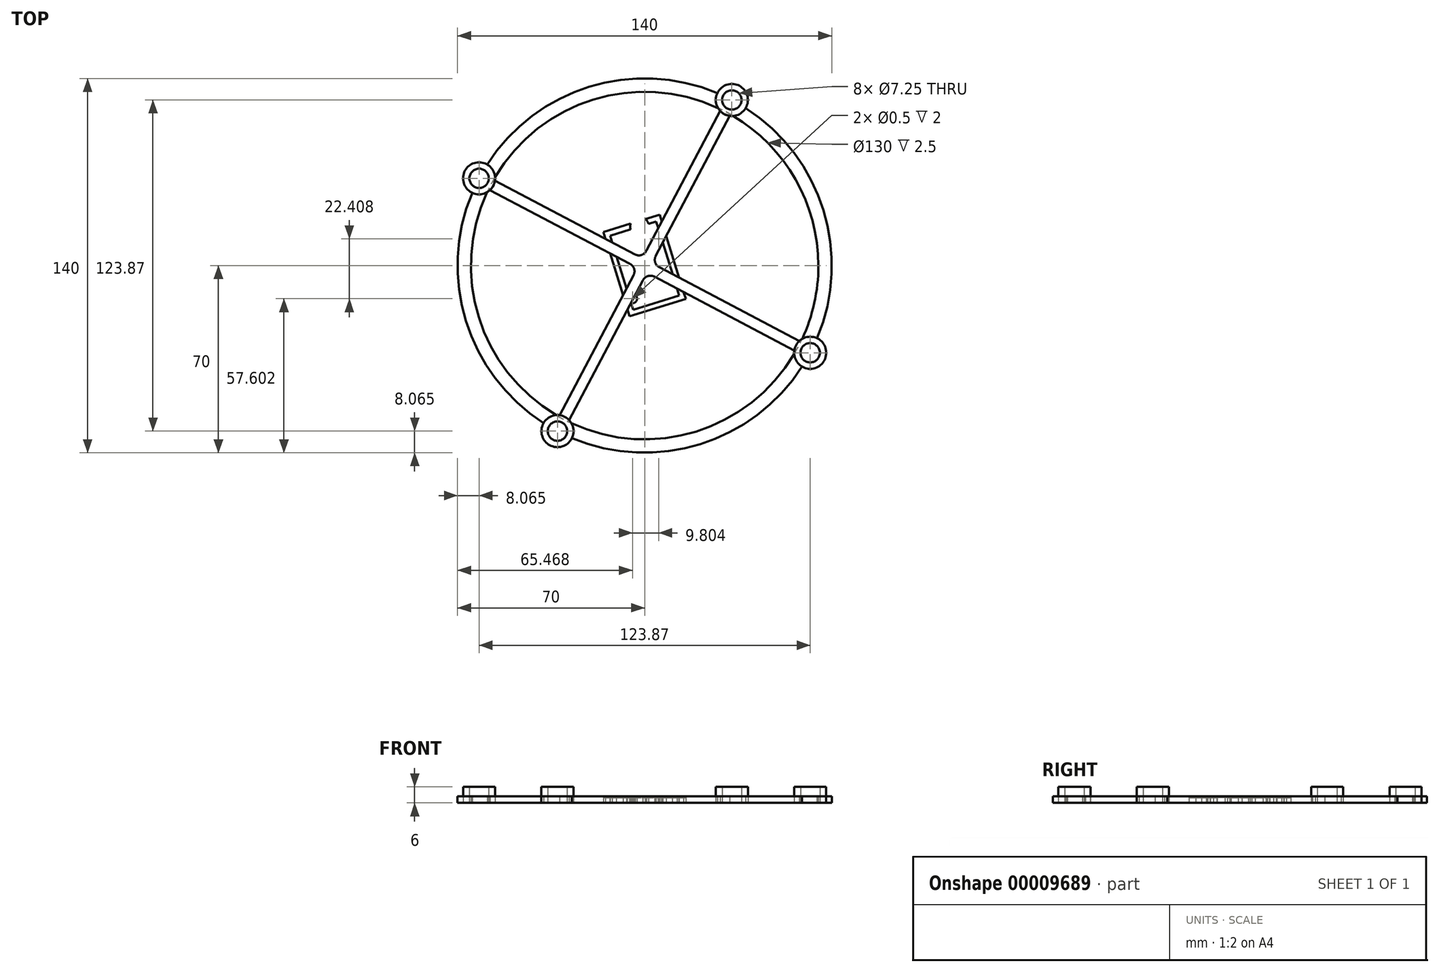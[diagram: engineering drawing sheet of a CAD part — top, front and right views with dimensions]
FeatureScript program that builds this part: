
annotation { "Feature Type Name" : "Feature", "Feature Type Description" : "" }
export const myFeature = defineFeature(function(context is Context, id is Id, definition is map)
    precondition{}
    {
        {
            var Q0;
            Q0=qCreatedBy(makeId("Top.planeOp"),FACE);
            var sketch = newSketch(context, id + "F0", { "sketchPlane" : qUnion([Q0])});
            skCircle(sketch, "E0", {"center": v(-61.93, 32.62) * mm, "radius": 3.62 * mm});
            skCircle(sketch, "E1", {"center": v(-61.93, 32.62) * mm, "radius": 6 * mm});
            skCircle(sketch, "E2", {"center": v(0, 0) * mm, "radius": 70 * mm});
            skCircle(sketch, "E3", {"center": v(0, 0) * mm, "radius": 65 * mm});
            skCircle(sketch, "E4.1.0", {"center": v(-32.62, -61.93) * mm, "radius": 3.62 * mm});
            skCircle(sketch, "E4.1.1", {"center": v(-32.62, -61.93) * mm, "radius": 6 * mm});
            skCircle(sketch, "E4.2.0", {"center": v(61.93, -32.62) * mm, "radius": 3.62 * mm});
            skCircle(sketch, "E4.2.1", {"center": v(61.93, -32.62) * mm, "radius": 6 * mm});
            skCircle(sketch, "E4.3.0", {"center": v(32.62, 61.93) * mm, "radius": 3.62 * mm});
            skCircle(sketch, "E4.3.1", {"center": v(32.62, 61.93) * mm, "radius": 6 * mm});
            skLineSegment(sketch, "E5", {"start": v(32.62, 61.93) * mm, "end": v(-32.62, -61.93) * mm});
            skLineSegment(sketch, "E6", {"start": v(-56.55, 32.05) * mm, "end": v(-3.59, 4.15) * mm});
            skArc(sketch, "E7", {"start": v(-3.59, 4.15) * mm, "mid": v(-1.1, 3.97) * mm, "end": v(0.72, 5.66) * mm});
            skLineSegment(sketch, "E8", {"start": v(0.72, 5.66) * mm, "end": v(28.5, 58.42) * mm});
            skLineSegment(sketch, "E9", {"start": v(61.93, -32.62) * mm, "end": v(-61.93, 32.62) * mm});
            skLineSegment(sketch, "E10.1.0", {"start": v(-5.66, 0.72) * mm, "end": v(-58.42, 28.5) * mm});
            skArc(sketch, "E10.1.1", {"start": v(-4.15, -3.59) * mm, "mid": v(-3.97, -1.1) * mm, "end": v(-5.66, 0.72) * mm});
            skLineSegment(sketch, "E10.1.2", {"start": v(-32.05, -56.55) * mm, "end": v(-4.15, -3.59) * mm});
            skLineSegment(sketch, "E10.2.0", {"start": v(-0.72, -5.66) * mm, "end": v(-28.5, -58.42) * mm});
            skArc(sketch, "E10.2.1", {"start": v(3.59, -4.15) * mm, "mid": v(1.1, -3.97) * mm, "end": v(-0.72, -5.66) * mm});
            skLineSegment(sketch, "E10.2.2", {"start": v(56.55, -32.05) * mm, "end": v(3.59, -4.15) * mm});
            skLineSegment(sketch, "E10.3.0", {"start": v(5.66, -0.72) * mm, "end": v(58.42, -28.5) * mm});
            skArc(sketch, "E10.3.1", {"start": v(4.15, 3.59) * mm, "mid": v(3.97, 1.1) * mm, "end": v(5.66, -0.72) * mm});
            skLineSegment(sketch, "E10.3.2", {"start": v(32.05, 56.55) * mm, "end": v(4.15, 3.59) * mm});
            skSolve(sketch);
        }
        {
            var Q0;
            {var subQ0=sQuery(id+"F0.wireOp",EDGE,"E2");var subQ1=sQuery(id+"F0.wireOp",EDGE,"E0");var subQ2=makeQuery(id+"F0.imprint","INTERSECT",VERTEX,{"disambiguationData":[OD(0.0)],"derivedFrom":[subQ1,subQ0]});Q0=makeQuery(id+"F0.imprint","IMPRINT",FACE,{"disambiguationData":[TD([[makeQuery(id+"F0.imprint","IMPRINT",EDGE,{"disambiguationData":[TD([[subQ2,1.0]])],"derivedFrom":subQ1}),-1.0]])]});}
            var Q1;
            {var subQ3=sQuery(id+"F0.wireOp",EDGE,"E0");var subQ8=sQuery(id+"F0.wireOp",EDGE,"E2");var subQ9=makeQuery(id+"F0.imprint","INTERSECT",VERTEX,{"disambiguationData":[OD(0.0)],"derivedFrom":[subQ3,subQ8]});Q1=makeQuery(id+"F0.imprint","IMPRINT",FACE,{"disambiguationData":[TD([[makeQuery(id+"F0.imprint","IMPRINT",EDGE,{"disambiguationData":[TD([[subQ9,-1.0]])],"derivedFrom":subQ3}),-1.0]])]});}
            var Q2;
            {var subQ3=sQuery(id+"F0.wireOp",EDGE,"E0");var subQ8=sQuery(id+"F0.wireOp",EDGE,"E2");var subQ9=makeQuery(id+"F0.imprint","INTERSECT",VERTEX,{"disambiguationData":[OD(1.0)],"derivedFrom":[subQ3,subQ8]});Q2=makeQuery(id+"F0.imprint","IMPRINT",FACE,{"disambiguationData":[TD([[makeQuery(id+"F0.imprint","IMPRINT",EDGE,{"disambiguationData":[TD([[subQ9,1.0]])],"derivedFrom":subQ3}),-1.0]])]});}
            var Q3;
            {var subQ0=sQuery(id+"F0.wireOp",EDGE,"E9");var subQ3=sQuery(id+"F0.wireOp",EDGE,"E1");var subQ4=makeQuery(id+"F0.imprint","INTERSECT",VERTEX,{"derivedFrom":[subQ3,subQ0]});Q3=makeQuery(id+"F0.imprint","IMPRINT",FACE,{"disambiguationData":[TD([[makeQuery(id+"F0.imprint","IMPRINT",EDGE,{"disambiguationData":[TD([[subQ4,-1.0]])],"derivedFrom":subQ3}),1.0]])]});}
            var Q4;
            {var subQ0=sQuery(id+"F0.wireOp",EDGE,"E10.1.0");var subQ1=sQuery(id+"F0.wireOp",EDGE,"E1");var subQ2=makeQuery(id+"F0.imprint","INTERSECT",VERTEX,{"derivedFrom":[subQ1,subQ0]});Q4=makeQuery(id+"F0.imprint","IMPRINT",FACE,{"disambiguationData":[TD([[makeQuery(id+"F0.imprint","IMPRINT",EDGE,{"disambiguationData":[TD([[subQ2,-1.0]])],"derivedFrom":subQ1}),1.0]])]});}
            var Q5;
            {var subQ1=sQuery(id+"F0.wireOp",EDGE,"E1");var subQ3=sQuery(id+"F0.wireOp",EDGE,"E3");var subQ5=makeQuery(id+"F0.imprint","INTERSECT",VERTEX,{"disambiguationData":[OD(0.0)],"derivedFrom":[subQ1,subQ3]});Q5=makeQuery(id+"F0.imprint","IMPRINT",FACE,{"disambiguationData":[TD([[makeQuery(id+"F0.imprint","IMPRINT",EDGE,{"disambiguationData":[TD([[subQ5,1.0]])],"derivedFrom":subQ1}),1.0]])]});}
            var Q6;
            {var subQ1=sQuery(id+"F0.wireOp",EDGE,"E1");var subQ3=sQuery(id+"F0.wireOp",EDGE,"E3");var subQ5=makeQuery(id+"F0.imprint","INTERSECT",VERTEX,{"disambiguationData":[OD(1.0)],"derivedFrom":[subQ1,subQ3]});Q6=makeQuery(id+"F0.imprint","IMPRINT",FACE,{"disambiguationData":[TD([[makeQuery(id+"F0.imprint","IMPRINT",EDGE,{"disambiguationData":[TD([[subQ5,-1.0]])],"derivedFrom":subQ1}),1.0]])]});}
            var Q7;
            {var subQ0=sQuery(id+"F0.wireOp",EDGE,"E4.3.1");var subQ1=sQuery(id+"F0.wireOp",EDGE,"E2");var subQ3=makeQuery(id+"F0.imprint","INTERSECT",VERTEX,{"disambiguationData":[OD(0.0)],"derivedFrom":[subQ1,subQ0]});Q7=makeQuery(id+"F0.imprint","IMPRINT",FACE,{"disambiguationData":[TD([[makeQuery(id+"F0.imprint","IMPRINT",EDGE,{"disambiguationData":[TD([[subQ3,-1.0]])],"derivedFrom":subQ1}),-1.0]])]});}
            var Q8;
            {var subQ5=sQuery(id+"F0.wireOp",EDGE,"E4.3.1");var subQ7=sQuery(id+"F0.wireOp",EDGE,"E2");var subQ8=makeQuery(id+"F0.imprint","INTERSECT",VERTEX,{"disambiguationData":[OD(0.0)],"derivedFrom":[subQ7,subQ5]});Q8=makeQuery(id+"F0.imprint","IMPRINT",FACE,{"disambiguationData":[TD([[makeQuery(id+"F0.imprint","IMPRINT",EDGE,{"disambiguationData":[TD([[subQ8,-1.0]])],"derivedFrom":subQ7}),1.0]])]});}
            var Q9;
            {var subQ0=sQuery(id+"F0.wireOp",EDGE,"E10.3.2");var subQ3=sQuery(id+"F0.wireOp",EDGE,"E3");var subQ4=makeQuery(id+"F0.imprint","INTERSECT",VERTEX,{"derivedFrom":[subQ3,subQ0]});Q9=makeQuery(id+"F0.imprint","IMPRINT",FACE,{"disambiguationData":[TD([[makeQuery(id+"F0.imprint","IMPRINT",EDGE,{"disambiguationData":[TD([[subQ4,-1.0]])],"derivedFrom":subQ3}),1.0]])]});}
            var Q10;
            {var subQ5=sQuery(id+"F0.wireOp",EDGE,"E4.3.1");var subQ7=sQuery(id+"F0.wireOp",EDGE,"E2");var subQ8=makeQuery(id+"F0.imprint","INTERSECT",VERTEX,{"disambiguationData":[OD(1.0)],"derivedFrom":[subQ7,subQ5]});Q10=makeQuery(id+"F0.imprint","IMPRINT",FACE,{"disambiguationData":[TD([[makeQuery(id+"F0.imprint","IMPRINT",EDGE,{"disambiguationData":[TD([[subQ8,1.0]])],"derivedFrom":subQ7}),1.0]])]});}
            var Q11;
            {var subQ0=sQuery(id+"F0.wireOp",EDGE,"E10.3.2");var subQ3=sQuery(id+"F0.wireOp",EDGE,"E3");var subQ4=makeQuery(id+"F0.imprint","INTERSECT",VERTEX,{"derivedFrom":[subQ3,subQ0]});Q11=makeQuery(id+"F0.imprint","IMPRINT",FACE,{"disambiguationData":[TD([[makeQuery(id+"F0.imprint","IMPRINT",EDGE,{"disambiguationData":[TD([[subQ4,1.0]])],"derivedFrom":subQ3}),1.0]])]});}
            var Q12;
            {var subQ0=sQuery(id+"F0.wireOp",EDGE,"E8");var subQ3=sQuery(id+"F0.wireOp",EDGE,"E3");var subQ4=makeQuery(id+"F0.imprint","INTERSECT",VERTEX,{"derivedFrom":[subQ3,subQ0]});Q12=makeQuery(id+"F0.imprint","IMPRINT",FACE,{"disambiguationData":[TD([[makeQuery(id+"F0.imprint","IMPRINT",EDGE,{"disambiguationData":[TD([[subQ4,1.0]])],"derivedFrom":subQ3}),1.0]])]});}
            var Q13;
            {var subQ0=sQuery(id+"F0.wireOp",EDGE,"E8");var subQ3=sQuery(id+"F0.wireOp",EDGE,"E3");var subQ4=makeQuery(id+"F0.imprint","INTERSECT",VERTEX,{"derivedFrom":[subQ3,subQ0]});Q13=makeQuery(id+"F0.imprint","IMPRINT",FACE,{"disambiguationData":[TD([[makeQuery(id+"F0.imprint","IMPRINT",EDGE,{"disambiguationData":[TD([[subQ4,-1.0]])],"derivedFrom":subQ3}),1.0]])]});}
            var Q14;
            {var subQ0=sQuery(id+"F0.wireOp",EDGE,"E4.2.1");var subQ1=sQuery(id+"F0.wireOp",EDGE,"E2");var subQ3=makeQuery(id+"F0.imprint","INTERSECT",VERTEX,{"disambiguationData":[OD(0.0)],"derivedFrom":[subQ1,subQ0]});Q14=makeQuery(id+"F0.imprint","IMPRINT",FACE,{"disambiguationData":[TD([[makeQuery(id+"F0.imprint","IMPRINT",EDGE,{"disambiguationData":[TD([[subQ3,-1.0]])],"derivedFrom":subQ1}),-1.0]])]});}
            var Q15;
            {var subQ5=sQuery(id+"F0.wireOp",EDGE,"E2");var subQ7=sQuery(id+"F0.wireOp",EDGE,"E4.2.1");var subQ10=makeQuery(id+"F0.imprint","INTERSECT",VERTEX,{"disambiguationData":[OD(1.0)],"derivedFrom":[subQ5,subQ7]});Q15=makeQuery(id+"F0.imprint","IMPRINT",FACE,{"disambiguationData":[TD([[makeQuery(id+"F0.imprint","IMPRINT",EDGE,{"disambiguationData":[TD([[subQ10,1.0]])],"derivedFrom":subQ5}),1.0]])]});}
            var Q16;
            {var subQ0=sQuery(id+"F0.wireOp",EDGE,"E10.3.0");var subQ3=sQuery(id+"F0.wireOp",EDGE,"E3");var subQ4=makeQuery(id+"F0.imprint","INTERSECT",VERTEX,{"derivedFrom":[subQ3,subQ0]});Q16=makeQuery(id+"F0.imprint","IMPRINT",FACE,{"disambiguationData":[TD([[makeQuery(id+"F0.imprint","IMPRINT",EDGE,{"disambiguationData":[TD([[subQ4,-1.0]])],"derivedFrom":subQ3}),1.0]])]});}
            var Q17;
            {var subQ0=sQuery(id+"F0.wireOp",EDGE,"E10.3.0");var subQ3=sQuery(id+"F0.wireOp",EDGE,"E3");var subQ4=makeQuery(id+"F0.imprint","INTERSECT",VERTEX,{"derivedFrom":[subQ3,subQ0]});Q17=makeQuery(id+"F0.imprint","IMPRINT",FACE,{"disambiguationData":[TD([[makeQuery(id+"F0.imprint","IMPRINT",EDGE,{"disambiguationData":[TD([[subQ4,1.0]])],"derivedFrom":subQ3}),1.0]])]});}
            var Q18;
            {var subQ0=sQuery(id+"F0.wireOp",EDGE,"E10.2.2");var subQ3=sQuery(id+"F0.wireOp",EDGE,"E3");var subQ4=makeQuery(id+"F0.imprint","INTERSECT",VERTEX,{"derivedFrom":[subQ3,subQ0]});Q18=makeQuery(id+"F0.imprint","IMPRINT",FACE,{"disambiguationData":[TD([[makeQuery(id+"F0.imprint","IMPRINT",EDGE,{"disambiguationData":[TD([[subQ4,-1.0]])],"derivedFrom":subQ3}),1.0]])]});}
            var Q19;
            {var subQ5=sQuery(id+"F0.wireOp",EDGE,"E4.2.1");var subQ7=sQuery(id+"F0.wireOp",EDGE,"E2");var subQ8=makeQuery(id+"F0.imprint","INTERSECT",VERTEX,{"disambiguationData":[OD(0.0)],"derivedFrom":[subQ7,subQ5]});Q19=makeQuery(id+"F0.imprint","IMPRINT",FACE,{"disambiguationData":[TD([[makeQuery(id+"F0.imprint","IMPRINT",EDGE,{"disambiguationData":[TD([[subQ8,-1.0]])],"derivedFrom":subQ7}),1.0]])]});}
            var Q20;
            {var subQ0=sQuery(id+"F0.wireOp",EDGE,"E10.2.2");var subQ3=sQuery(id+"F0.wireOp",EDGE,"E3");var subQ4=makeQuery(id+"F0.imprint","INTERSECT",VERTEX,{"derivedFrom":[subQ3,subQ0]});Q20=makeQuery(id+"F0.imprint","IMPRINT",FACE,{"disambiguationData":[TD([[makeQuery(id+"F0.imprint","IMPRINT",EDGE,{"disambiguationData":[TD([[subQ4,1.0]])],"derivedFrom":subQ3}),1.0]])]});}
            var Q21;
            {var subQ5=sQuery(id+"F0.wireOp",EDGE,"E4.1.1");var subQ7=sQuery(id+"F0.wireOp",EDGE,"E2");var subQ8=makeQuery(id+"F0.imprint","INTERSECT",VERTEX,{"disambiguationData":[OD(1.0)],"derivedFrom":[subQ7,subQ5]});Q21=makeQuery(id+"F0.imprint","IMPRINT",FACE,{"disambiguationData":[TD([[makeQuery(id+"F0.imprint","IMPRINT",EDGE,{"disambiguationData":[TD([[subQ8,1.0]])],"derivedFrom":subQ7}),1.0]])]});}
            var Q22;
            {var subQ0=sQuery(id+"F0.wireOp",EDGE,"E10.2.0");var subQ3=sQuery(id+"F0.wireOp",EDGE,"E3");var subQ4=makeQuery(id+"F0.imprint","INTERSECT",VERTEX,{"derivedFrom":[subQ3,subQ0]});Q22=makeQuery(id+"F0.imprint","IMPRINT",FACE,{"disambiguationData":[TD([[makeQuery(id+"F0.imprint","IMPRINT",EDGE,{"disambiguationData":[TD([[subQ4,1.0]])],"derivedFrom":subQ3}),1.0]])]});}
            var Q23;
            {var subQ0=sQuery(id+"F0.wireOp",EDGE,"E10.2.0");var subQ3=sQuery(id+"F0.wireOp",EDGE,"E3");var subQ4=makeQuery(id+"F0.imprint","INTERSECT",VERTEX,{"derivedFrom":[subQ3,subQ0]});Q23=makeQuery(id+"F0.imprint","IMPRINT",FACE,{"disambiguationData":[TD([[makeQuery(id+"F0.imprint","IMPRINT",EDGE,{"disambiguationData":[TD([[subQ4,-1.0]])],"derivedFrom":subQ3}),1.0]])]});}
            var Q24;
            {var subQ0=sQuery(id+"F0.wireOp",EDGE,"E10.1.2");var subQ3=sQuery(id+"F0.wireOp",EDGE,"E3");var subQ4=makeQuery(id+"F0.imprint","INTERSECT",VERTEX,{"derivedFrom":[subQ3,subQ0]});Q24=makeQuery(id+"F0.imprint","IMPRINT",FACE,{"disambiguationData":[TD([[makeQuery(id+"F0.imprint","IMPRINT",EDGE,{"disambiguationData":[TD([[subQ4,-1.0]])],"derivedFrom":subQ3}),1.0]])]});}
            var Q25;
            {var subQ0=sQuery(id+"F0.wireOp",EDGE,"E10.1.2");var subQ3=sQuery(id+"F0.wireOp",EDGE,"E3");var subQ4=makeQuery(id+"F0.imprint","INTERSECT",VERTEX,{"derivedFrom":[subQ3,subQ0]});Q25=makeQuery(id+"F0.imprint","IMPRINT",FACE,{"disambiguationData":[TD([[makeQuery(id+"F0.imprint","IMPRINT",EDGE,{"disambiguationData":[TD([[subQ4,1.0]])],"derivedFrom":subQ3}),1.0]])]});}
            var Q26;
            {var subQ0=sQuery(id+"F0.wireOp",EDGE,"E4.1.1");var subQ3=sQuery(id+"F0.wireOp",EDGE,"E2");var subQ4=makeQuery(id+"F0.imprint","INTERSECT",VERTEX,{"disambiguationData":[OD(0.0)],"derivedFrom":[subQ3,subQ0]});Q26=makeQuery(id+"F0.imprint","IMPRINT",FACE,{"disambiguationData":[TD([[makeQuery(id+"F0.imprint","IMPRINT",EDGE,{"disambiguationData":[TD([[subQ4,-1.0]])],"derivedFrom":subQ3}),1.0]])]});}
            var Q27;
            {var subQ1=sQuery(id+"F0.wireOp",EDGE,"E2");var subQ4=sQuery(id+"F0.wireOp",EDGE,"E4.1.1");var subQ6=makeQuery(id+"F0.imprint","INTERSECT",VERTEX,{"disambiguationData":[OD(0.0)],"derivedFrom":[subQ1,subQ4]});Q27=makeQuery(id+"F0.imprint","IMPRINT",FACE,{"disambiguationData":[TD([[makeQuery(id+"F0.imprint","IMPRINT",EDGE,{"disambiguationData":[TD([[subQ6,-1.0]])],"derivedFrom":subQ1}),-1.0]])]});}
            extrude(context, id + "F1", {"entities" : qUnion([Q0, Q1, Q2, Q3, Q4, Q5, Q6, Q7, Q8, Q9, Q10, Q11, Q12, Q13, Q14, Q15, Q16, Q17, Q18, Q19, Q20, Q21, Q22, Q23, Q24, Q25, Q26, Q27]), "depth" : 6 * mm});
        }
        {
            var Q0;
            Q0 = qSketchRegion(id + "F0", true);
            var Q1;
            {var subQ3=sQuery(id+"F0.wireOp",EDGE,"E10.3.1");Q1=makeQuery(id+"F0.imprint","IMPRINT",FACE,{"disambiguationData":[TD([[makeQuery(id+"F0.imprint","IMPRINT",EDGE,{"derivedFrom":subQ3}),-1.0]])]});}
            var Q2;
            {var subQ3=sQuery(id+"F0.wireOp",EDGE,"E7");Q2=makeQuery(id+"F0.imprint","IMPRINT",FACE,{"disambiguationData":[TD([[makeQuery(id+"F0.imprint","IMPRINT",EDGE,{"derivedFrom":subQ3}),-1.0]])]});}
            var Q3;
            {var subQ3=sQuery(id+"F0.wireOp",EDGE,"E10.1.1");Q3=makeQuery(id+"F0.imprint","IMPRINT",FACE,{"disambiguationData":[TD([[makeQuery(id+"F0.imprint","IMPRINT",EDGE,{"derivedFrom":subQ3}),-1.0]])]});}
            var Q4;
            {var subQ3=sQuery(id+"F0.wireOp",EDGE,"E10.2.1");Q4=makeQuery(id+"F0.imprint","IMPRINT",FACE,{"disambiguationData":[TD([[makeQuery(id+"F0.imprint","IMPRINT",EDGE,{"derivedFrom":subQ3}),-1.0]])]});}
            extrude(context, id + "F2", {"entities" : qUnion([Q0, Q1, Q2, Q3, Q4]), "depth" : 2.5 * mm});
        }
        {
            var Q0;
            {var subQ3=sQuery(id+"F0.wireOp",EDGE,"E10.3.1");Q0=makeQuery(id+"F0.imprint","IMPRINT",FACE,{"disambiguationData":[TD([[makeQuery(id+"F0.imprint","IMPRINT",EDGE,{"derivedFrom":subQ3}),-1.0]])]});}
            var sketch = newSketch(context, id + "F3", { "sketchPlane" : qUnion([Q0])});
            skLineSegment(sketch, "E11", {"start": v(-32.62, -61.93) * mm, "end": v(-61.93, 32.62) * mm, "construction": true});
            skLineSegment(sketch, "E12", {"start": v(-61.93, 32.62) * mm, "end": v(32.62, 61.93) * mm, "construction": true});
            skLineSegment(sketch, "E13", {"start": v(32.62, 61.93) * mm, "end": v(61.93, -32.62) * mm, "construction": true});
            skLineSegment(sketch, "E14", {"start": v(61.93, -32.62) * mm, "end": v(-32.62, -61.93) * mm, "construction": true});
            skLineSegment(sketch, "E15", {"start": v(-4.3, -16.51) * mm, "end": v(12.9, -11.18) * mm});
            skLineSegment(sketch, "E16", {"start": v(12.9, -11.18) * mm, "end": v(4.3, 16.51) * mm});
            skLineSegment(sketch, "E17", {"start": v(4.3, 16.51) * mm, "end": v(-12.9, 11.18) * mm});
            skLineSegment(sketch, "E18", {"start": v(-12.9, 11.18) * mm, "end": v(-4.3, -16.51) * mm});
            skLineSegment(sketch, "E19.0", {"start": v(-15.4, 12.5) * mm, "end": v(-5.62, -19.02) * mm});
            skLineSegment(sketch, "E19.1", {"start": v(5.62, 19.02) * mm, "end": v(-15.4, 12.5) * mm});
            skLineSegment(sketch, "E19.2", {"start": v(15.4, -12.5) * mm, "end": v(5.62, 19.02) * mm});
            skLineSegment(sketch, "E19.3", {"start": v(-5.62, -19.02) * mm, "end": v(15.4, -12.5) * mm});
            skCircle(sketch, "E20", {"center": v(-1.9, 14.59) * mm, "radius": 3.5 * mm});
            skCircle(sketch, "E21", {"center": v(-1.9, 14.59) * mm, "radius": 5.5 * mm});
            skCircle(sketch, "E22", {"center": v(-4.53, -12.4) * mm, "radius": 1.7 * mm});
            skCircle(sketch, "E23", {"center": v(-4.53, -12.4) * mm, "radius": 0.25 * mm});
            skLineSegment(sketch, "E24", {"start": v(-4.03, -14.02) * mm, "end": v(-4.98, -14.32) * mm});
            skLineSegment(sketch, "E25", {"start": v(-5.04, -10.77) * mm, "end": v(-6, -11.07) * mm});
            skCircle(sketch, "E26", {"center": v(5.27, 10.01) * mm, "radius": 1.7 * mm});
            skCircle(sketch, "E27", {"center": v(5.27, 10.01) * mm, "radius": 0.25 * mm});
            skLineSegment(sketch, "E28", {"start": v(5.78, 8.39) * mm, "end": v(6.73, 8.68) * mm});
            skLineSegment(sketch, "E29", {"start": v(4.77, 11.63) * mm, "end": v(5.72, 11.93) * mm});
            skSolve(sketch);
        }
        {
            var Q0;
            Q0=makeQuery(id+"F3.imprint","IMPRINT",FACE,{"disambiguationData":[TD([[makeQuery(id+"F3.imprint","IMPRINT",EDGE,{"derivedFrom":sQuery(id+"F3.wireOp",EDGE,"E23")}),1.0]])]});
            var Q1;
            {var subQ0=sQuery(id+"F0.wireOp",EDGE,"E5");var subQ1=makeQuery(id+"F0.imprint","IMPRINT",EDGE,{"disambiguationData":[TD([[makeQuery(id+"F0.imprint","INTERSECT",VERTEX,{"derivedFrom":[sQuery(id+"F0.wireOp",EDGE,"E4.3.1"),subQ0]}),-1.0]])],"derivedFrom":subQ0});var subQ2=sQuery(id+"F3.wireOp",EDGE,"E27");var subQ4=makeQuery(id+"F3.imprint","INTERSECT",VERTEX,{"disambiguationData":[OD(0.0)],"derivedFrom":[subQ1,subQ2]});Q1=makeQuery(id+"F3.imprint","IMPRINT",FACE,{"disambiguationData":[TD([[makeQuery(id+"F3.imprint","IMPRINT",EDGE,{"disambiguationData":[TD([[subQ4,-1.0]])],"derivedFrom":subQ2}),1.0]])]});}
            var Q2;
            {var subQ0=sQuery(id+"F0.wireOp",EDGE,"E5");var subQ1=makeQuery(id+"F0.imprint","IMPRINT",EDGE,{"disambiguationData":[TD([[makeQuery(id+"F0.imprint","INTERSECT",VERTEX,{"derivedFrom":[sQuery(id+"F0.wireOp",EDGE,"E4.3.1"),subQ0]}),-1.0]])],"derivedFrom":subQ0});var subQ2=sQuery(id+"F3.wireOp",EDGE,"E27");var subQ4=makeQuery(id+"F3.imprint","INTERSECT",VERTEX,{"disambiguationData":[OD(0.0)],"derivedFrom":[subQ1,subQ2]});Q2=makeQuery(id+"F3.imprint","IMPRINT",FACE,{"disambiguationData":[TD([[makeQuery(id+"F3.imprint","IMPRINT",EDGE,{"disambiguationData":[TD([[subQ4,1.0]])],"derivedFrom":subQ2}),1.0]])]});}
            extrude(context, id + "F4", {"entities" : qUnion([Q0, Q1, Q2]), "operationType" : NewBodyOperationType.REMOVE, "depth" : 2 * mm});
        }
        {
            var Q0;
            {var subQ18=sQuery(id+"F3.wireOp",EDGE,"E15");Q0=makeQuery(id+"F3.imprint","IMPRINT",FACE,{"disambiguationData":[TD([[makeQuery(id+"F3.imprint","IMPRINT",EDGE,{"derivedFrom":subQ18}),-1.0]])]});}
            var Q1;
            {var subQ1=sQuery(id+"F3.wireOp",EDGE,"E17");var subQ5=sQuery(id+"F3.wireOp",EDGE,"E20");var subQ7=makeQuery(id+"F3.imprint","INTERSECT",VERTEX,{"disambiguationData":[OD(1.0)],"derivedFrom":[subQ1,subQ5]});Q1=makeQuery(id+"F3.imprint","IMPRINT",FACE,{"disambiguationData":[TD([[makeQuery(id+"F3.imprint","IMPRINT",EDGE,{"disambiguationData":[TD([[subQ7,-1.0]])],"derivedFrom":subQ1}),-1.0]])]});}
            var Q2;
            {var subQ0=sQuery(id+"F3.wireOp",EDGE,"E21");var subQ1=sQuery(id+"F3.wireOp",EDGE,"E19.1");var subQ3=makeQuery(id+"F3.imprint","INTERSECT",VERTEX,{"disambiguationData":[OD(0.0)],"derivedFrom":[subQ1,subQ0]});Q2=makeQuery(id+"F3.imprint","IMPRINT",FACE,{"disambiguationData":[TD([[makeQuery(id+"F3.imprint","IMPRINT",EDGE,{"disambiguationData":[TD([[subQ3,-1.0]])],"derivedFrom":subQ1}),-1.0]])]});}
            var Q3;
            {var subQ0=sQuery(id+"F3.wireOp",EDGE,"E21");var subQ1=sQuery(id+"F3.wireOp",EDGE,"E17");var subQ2=makeQuery(id+"F3.imprint","INTERSECT",VERTEX,{"disambiguationData":[OD(0.0)],"derivedFrom":[subQ1,subQ0]});Q3=makeQuery(id+"F3.imprint","IMPRINT",FACE,{"disambiguationData":[TD([[makeQuery(id+"F3.imprint","IMPRINT",EDGE,{"disambiguationData":[TD([[subQ2,-1.0]])],"derivedFrom":subQ1}),-1.0]])]});}
            var Q4;
            {var subQ12=sQuery(id+"F3.wireOp",EDGE,"E16");var subQ15=makeQuery(id+"F3.imprint","INTERSECT",VERTEX,{"derivedFrom":[subQ12,sQuery(id+"F3.wireOp",EDGE,"E29")]});Q4=makeQuery(id+"F3.imprint","IMPRINT",FACE,{"disambiguationData":[TD([[makeQuery(id+"F3.imprint","IMPRINT",EDGE,{"disambiguationData":[TD([[subQ15,1.0]])],"derivedFrom":subQ12}),-1.0]])]});}
            var Q5;
            {var subQ0=sQuery(id+"F0.wireOp",EDGE,"E10.3.0");var subQ1=sQuery(id+"F0.wireOp",EDGE,"E10.3.1");var subQ2=makeQuery(id+"F0.imprint","IMPRINT",EDGE,{"disambiguationData":[TD([[makeQuery(id+"F0.imprint","INTERSECT",VERTEX,{"derivedFrom":[subQ0,subQ1]}),-1.0]])],"derivedFrom":subQ0});var subQ3=sQuery(id+"F3.wireOp",EDGE,"E16");var subQ4=makeQuery(id+"F3.imprint","INTERSECT",VERTEX,{"derivedFrom":[subQ2,subQ3]});Q5=makeQuery(id+"F3.imprint","IMPRINT",FACE,{"disambiguationData":[TD([[makeQuery(id+"F3.imprint","IMPRINT",EDGE,{"disambiguationData":[TD([[subQ4,-1.0]])],"derivedFrom":subQ3}),-1.0]])]});}
            var Q6;
            {var subQ0=sQuery(id+"F0.wireOp",EDGE,"E9");var subQ1=sQuery(id+"F0.wireOp",EDGE,"E4.2.1");var subQ2=makeQuery(id+"F0.imprint","IMPRINT",EDGE,{"disambiguationData":[TD([[makeQuery(id+"F0.imprint","INTERSECT",VERTEX,{"derivedFrom":[subQ1,subQ0]}),-1.0]])],"derivedFrom":subQ0});var subQ3=sQuery(id+"F3.wireOp",EDGE,"E16");var subQ4=makeQuery(id+"F3.imprint","INTERSECT",VERTEX,{"derivedFrom":[subQ2,subQ3]});Q6=makeQuery(id+"F3.imprint","IMPRINT",FACE,{"disambiguationData":[TD([[makeQuery(id+"F3.imprint","IMPRINT",EDGE,{"disambiguationData":[TD([[subQ4,-1.0]])],"derivedFrom":subQ3}),-1.0]])]});}
            var Q7;
            {var subQ9=sQuery(id+"F3.wireOp",EDGE,"E16");var subQ13=makeQuery(id+"F3.imprint","INTERSECT",VERTEX,{"derivedFrom":[subQ9,sQuery(id+"F3.wireOp",EDGE,"E28")]});Q7=makeQuery(id+"F3.imprint","IMPRINT",FACE,{"disambiguationData":[TD([[makeQuery(id+"F3.imprint","IMPRINT",EDGE,{"disambiguationData":[TD([[subQ13,-1.0]])],"derivedFrom":subQ9}),-1.0]])]});}
            var Q8;
            {var subQ2=sQuery(id+"F3.wireOp",EDGE,"E26");var subQ4=sQuery(id+"F3.wireOp",EDGE,"E16");var subQ6=makeQuery(id+"F3.imprint","INTERSECT",VERTEX,{"disambiguationData":[OD(0.0)],"derivedFrom":[subQ4,subQ2]});Q8=makeQuery(id+"F3.imprint","IMPRINT",FACE,{"disambiguationData":[TD([[makeQuery(id+"F3.imprint","IMPRINT",EDGE,{"disambiguationData":[TD([[subQ6,-1.0]])],"derivedFrom":subQ4}),-1.0]])]});}
            var Q9;
            {var subQ7=sQuery(id+"F3.wireOp",EDGE,"E26");var subQ9=makeQuery(id+"F3.imprint","INTERSECT",VERTEX,{"derivedFrom":[subQ7,sQuery(id+"F3.wireOp",EDGE,"E29")]});Q9=makeQuery(id+"F3.imprint","IMPRINT",FACE,{"disambiguationData":[TD([[makeQuery(id+"F3.imprint","IMPRINT",EDGE,{"disambiguationData":[TD([[subQ9,1.0]])],"derivedFrom":subQ7}),1.0]])]});}
            var Q10;
            {var subQ4=sQuery(id+"F3.wireOp",EDGE,"E26");var subQ9=makeQuery(id+"F3.imprint","INTERSECT",VERTEX,{"derivedFrom":[subQ4,sQuery(id+"F3.wireOp",EDGE,"E28")]});Q10=makeQuery(id+"F3.imprint","IMPRINT",FACE,{"disambiguationData":[TD([[makeQuery(id+"F3.imprint","IMPRINT",EDGE,{"disambiguationData":[TD([[subQ9,-1.0]])],"derivedFrom":subQ4}),1.0]])]});}
            var Q11;
            {var subQ0=sQuery(id+"F3.wireOp",EDGE,"E28");Q11=makeQuery(id+"F3.imprint","IMPRINT",FACE,{"disambiguationData":[TD([[makeQuery(id+"F3.imprint","IMPRINT",EDGE,{"derivedFrom":subQ0}),1.0]])]});}
            var Q12;
            {var subQ0=sQuery(id+"F3.wireOp",EDGE,"E25");Q12=makeQuery(id+"F3.imprint","IMPRINT",FACE,{"disambiguationData":[TD([[makeQuery(id+"F3.imprint","IMPRINT",EDGE,{"derivedFrom":subQ0}),1.0]])]});}
            var Q13;
            Q13=makeQuery(id+"F3.imprint","IMPRINT",FACE,{"disambiguationData":[TD([[makeQuery(id+"F3.imprint","IMPRINT",EDGE,{"derivedFrom":sQuery(id+"F3.wireOp",EDGE,"E23")}),-1.0]])]});
            var Q14;
            {var subQ0=sQuery(id+"F3.wireOp",EDGE,"E22");var subQ1=sQuery(id+"F3.wireOp",EDGE,"E18");var subQ3=makeQuery(id+"F3.imprint","INTERSECT",VERTEX,{"disambiguationData":[OD(0.0)],"derivedFrom":[subQ1,subQ0]});Q14=makeQuery(id+"F3.imprint","IMPRINT",FACE,{"disambiguationData":[TD([[makeQuery(id+"F3.imprint","IMPRINT",EDGE,{"disambiguationData":[TD([[subQ3,-1.0]])],"derivedFrom":subQ1}),-1.0]])]});}
            var Q15;
            {var subQ0=sQuery(id+"F3.wireOp",EDGE,"E29");Q15=makeQuery(id+"F3.imprint","IMPRINT",FACE,{"disambiguationData":[TD([[makeQuery(id+"F3.imprint","IMPRINT",EDGE,{"derivedFrom":subQ0}),-1.0]])]});}
            var Q16;
            {var subQ2=sQuery(id+"F3.wireOp",EDGE,"E26");var subQ4=sQuery(id+"F3.wireOp",EDGE,"E16");var subQ6=makeQuery(id+"F3.imprint","INTERSECT",VERTEX,{"disambiguationData":[OD(1.0)],"derivedFrom":[subQ4,subQ2]});Q16=makeQuery(id+"F3.imprint","IMPRINT",FACE,{"disambiguationData":[TD([[makeQuery(id+"F3.imprint","IMPRINT",EDGE,{"disambiguationData":[TD([[subQ6,1.0]])],"derivedFrom":subQ4}),-1.0]])]});}
            var Q17;
            {var subQ0=sQuery(id+"F3.wireOp",EDGE,"E24");Q17=makeQuery(id+"F3.imprint","IMPRINT",FACE,{"disambiguationData":[TD([[makeQuery(id+"F3.imprint","IMPRINT",EDGE,{"derivedFrom":subQ0}),-1.0]])]});}
            extrude(context, id + "F5", {"entities" : qUnion([Q0, Q1, Q2, Q3, Q4, Q5, Q6, Q7, Q8, Q9, Q10, Q11, Q12, Q13, Q14, Q15, Q16, Q17]), "operationType" : NewBodyOperationType.ADD, "depth" : 2 * mm});
        }
    });
